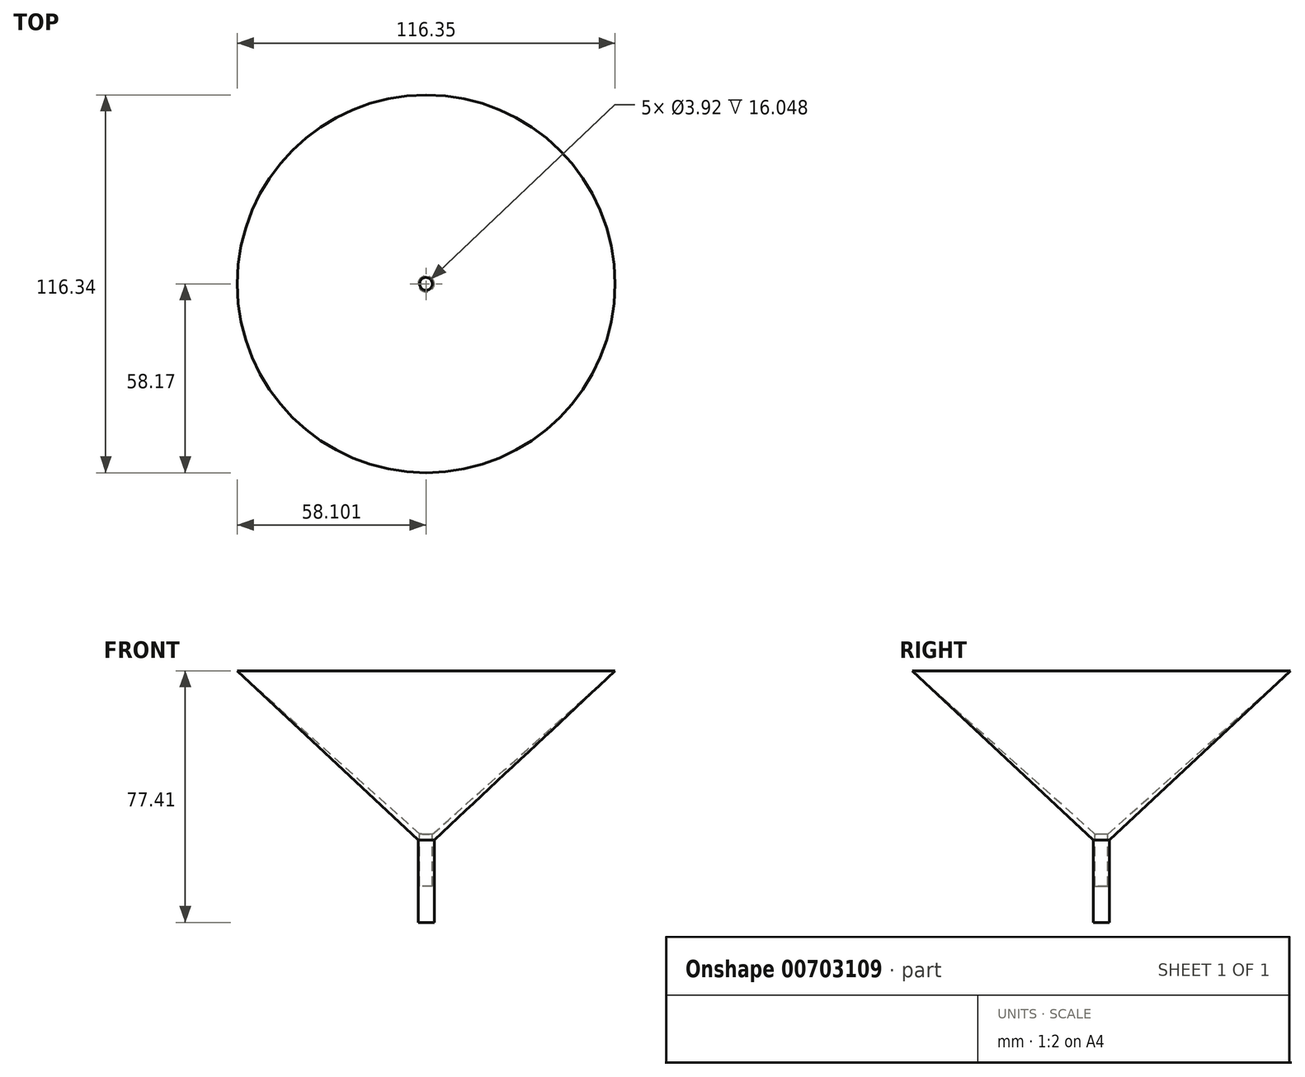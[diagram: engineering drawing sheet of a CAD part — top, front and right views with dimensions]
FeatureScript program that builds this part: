
annotation { "Feature Type Name" : "Feature", "Feature Type Description" : "" }
export const myFeature = defineFeature(function(context is Context, id is Id, definition is map)
    precondition{}
    {
        {
            var Q0;
            Q0=qCreatedBy(makeId("Front.planeOp"),FACE);
            var sketch = newSketch(context, id + "F0", { "sketchPlane" : qUnion([Q0])});
            skLineSegment(sketch, "E0", {"start": v(0, -36.57) * mm, "end": v(5.63, -36.57) * mm});
            skLineSegment(sketch, "E1", {"start": v(5.63, -36.57) * mm, "end": v(5.63, -11.17) * mm});
            skLineSegment(sketch, "E2", {"start": v(5.63, -11.17) * mm, "end": v(61.33, 40.84) * mm});
            skLineSegment(sketch, "E3", {"start": v(61.33, 40.84) * mm, "end": v(3.15, -11.17) * mm});
            skLineSegment(sketch, "E4", {"start": v(3.15, -11.17) * mm, "end": v(3.15, -36.57) * mm});
            skLineSegment(sketch, "E5", {"start": v(3.15, -36.57) * mm, "end": v(5.63, -36.57) * mm});
            skSolve(sketch);
        }
        {
            var Q0;
            Q0=makeQuery(id+"F0.imprint","IMPRINT",FACE,{"disambiguationData":[TD([[makeQuery(id+"F0.imprint","IMPRINT",EDGE,{"derivedFrom":sQuery(id+"F0.wireOp",EDGE,"E1")}),1.0]])]});
            var Q1;
            Q1=sQuery(id+"F0.wireOp",EDGE,"E4");
            revolve(context, id + "F1", {"surfaceOperationType" : NewSurfaceOperationType.NEW, "entities" : qUnion([Q0]), "axis" : qUnion([Q1]), "revolveType" : RevolveType.FULL});
        }
        {
            var Q0;
            Q0=qCreatedBy(makeId("Top.planeOp"),FACE);
            var sketch = newSketch(context, id + "F2", { "sketchPlane" : qUnion([Q0])});
            skCircle(sketch, "E6", {"center": v(3.08, 0) * mm, "radius": 1.96 * mm});
            skSolve(sketch);
        }
        {
            var Q0;
            Q0 = qSketchRegion(id + "F2", true);
            extrude(context, id + "F3", {"entities" : qUnion([Q0]), "operationType" : NewBodyOperationType.REMOVE, "oppositeDirection" : true, "depth" : 25.4 * mm, "offsetDistance" : 25.4 * mm});
        }
    });
